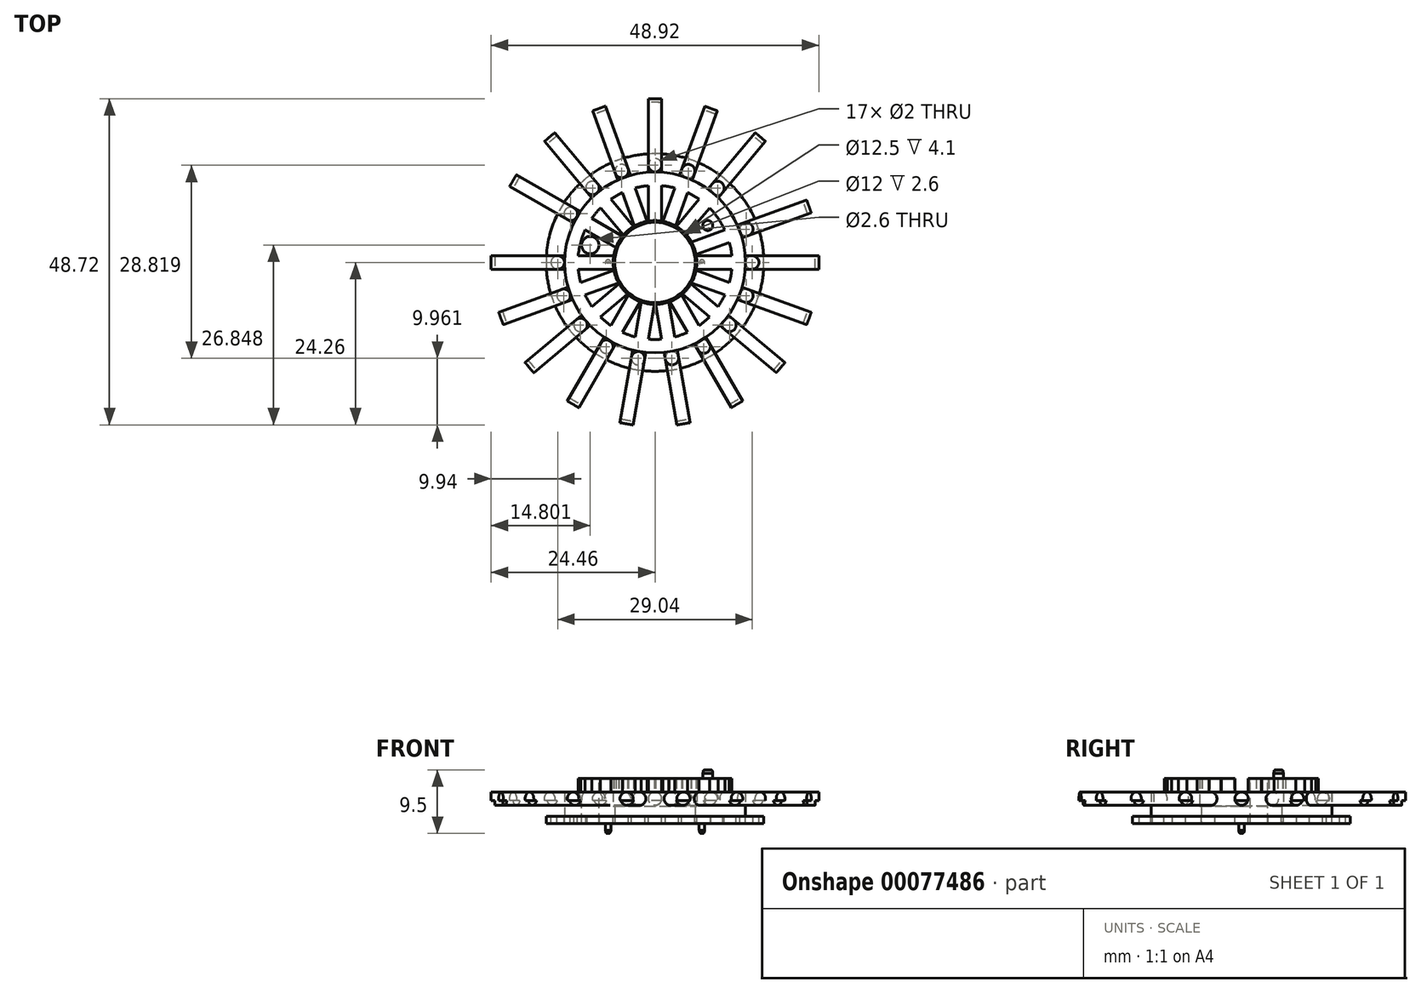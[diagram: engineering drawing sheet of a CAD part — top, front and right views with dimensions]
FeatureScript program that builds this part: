
annotation { "Feature Type Name" : "Feature", "Feature Type Description" : "" }
export const myFeature = defineFeature(function(context is Context, id is Id, definition is map)
    precondition{}
    {
        {
            var Q0;
            Q0=qCreatedBy(makeId("Front.planeOp"),FACE);
            var sketch = newSketch(context, id + "F0", { "sketchPlane" : qUnion([Q0])});
            skLineSegment(sketch, "E0", {"start": v(6, 0) * mm, "end": v(16.25, 0) * mm});
            skLineSegment(sketch, "E1", {"start": v(16.25, 0) * mm, "end": v(16.25, 1.1) * mm});
            skLineSegment(sketch, "E2", {"start": v(16.25, 1.1) * mm, "end": v(13.5, 1.1) * mm});
            skLineSegment(sketch, "E3", {"start": v(13.5, 1.1) * mm, "end": v(13.5, 4.7) * mm});
            skLineSegment(sketch, "E4", {"start": v(13.5, 4.7) * mm, "end": v(11.5, 4.7) * mm});
            skLineSegment(sketch, "E5", {"start": v(11.5, 4.7) * mm, "end": v(11.5, 6.7) * mm});
            skLineSegment(sketch, "E6", {"start": v(11.5, 6.7) * mm, "end": v(6.25, 6.7) * mm});
            skLineSegment(sketch, "E7", {"start": v(6.25, 6.7) * mm, "end": v(6.25, 2.6) * mm});
            skLineSegment(sketch, "E8", {"start": v(6.25, 2.6) * mm, "end": v(6, 2.6) * mm});
            skLineSegment(sketch, "E9", {"start": v(6, 2.6) * mm, "end": v(6, 0) * mm});
            skLineSegment(sketch, "E10", {"start": v(0, 0) * mm, "end": v(0, 6.7) * mm, "construction": true});
            skSolve(sketch);
        }
        {
            var Q0;
            Q0=makeQuery(id+"F0.imprint","IMPRINT",FACE,{"disambiguationData":[TD([[makeQuery(id+"F0.imprint","IMPRINT",EDGE,{"derivedFrom":sQuery(id+"F0.wireOp",EDGE,"E0")}),1.0]])]});
            var Q1;
            Q1=sQuery(id+"F0.wireOp",EDGE,"E10");
            revolve(context, id + "F1", {"entities" : qUnion([Q0]), "axis" : qUnion([Q1]), "revolveType" : RevolveType.FULL});
        }
        {
            var Q0;
            Q0=makeQuery(id+"F1.opRevolve","SWEPT_FACE",FACE,{"disambiguationData":[OSD([sQuery(id+"F0.wireOp",EDGE,"E6")])]});
            cPlane(context, id + "F2", {"entities" : qUnion([Q0]), "cplaneType" : CPlaneType.OFFSET, "offset" : 2 * mm, "oppositeDirection" : true, "width" : 150 * mm, "height" : 150 * mm});
        }
        {
            var Q0;
            Q0=qCreatedBy(id+"F2.planeOp",FACE);
            var sketch = newSketch(context, id + "F3", { "sketchPlane" : qUnion([Q0])});
            skLineSegment(sketch, "E11", {"start": v(-5, 1) * mm, "end": v(-15, 1) * mm});
            skLineSegment(sketch, "E12", {"start": v(-15, 1) * mm, "end": v(-15, -1) * mm});
            skLineSegment(sketch, "E13", {"start": v(-15, -1) * mm, "end": v(-5, -1) * mm});
            skLineSegment(sketch, "E14", {"start": v(-5, 1) * mm, "end": v(-5, -1) * mm});
            skLineSegment(sketch, "E15.1.0", {"start": v(-5.04, -0.77) * mm, "end": v(-14.44, -4.2) * mm});
            skLineSegment(sketch, "E15.1.1", {"start": v(-13.75, -6.07) * mm, "end": v(-4.36, -2.65) * mm});
            skLineSegment(sketch, "E15.1.2", {"start": v(-14.44, -4.2) * mm, "end": v(-13.75, -6.07) * mm});
            skLineSegment(sketch, "E15.1.3", {"start": v(-5.04, -0.77) * mm, "end": v(-4.36, -2.65) * mm});
            skLineSegment(sketch, "E15.2.0", {"start": v(-4.47, -2.45) * mm, "end": v(-12.13, -8.88) * mm});
            skLineSegment(sketch, "E15.2.1", {"start": v(-10.85, -10.4) * mm, "end": v(-3.19, -3.98) * mm});
            skLineSegment(sketch, "E15.2.2", {"start": v(-12.13, -8.88) * mm, "end": v(-10.85, -10.4) * mm});
            skLineSegment(sketch, "E15.2.3", {"start": v(-4.47, -2.45) * mm, "end": v(-3.19, -3.98) * mm});
            skLineSegment(sketch, "E15.3.0", {"start": v(-3.37, -3.83) * mm, "end": v(-8.37, -12.5) * mm});
            skLineSegment(sketch, "E15.3.1", {"start": v(-6.63, -13.5) * mm, "end": v(-1.63, -4.83) * mm});
            skLineSegment(sketch, "E15.3.2", {"start": v(-8.37, -12.5) * mm, "end": v(-6.63, -13.5) * mm});
            skLineSegment(sketch, "E15.3.3", {"start": v(-3.37, -3.83) * mm, "end": v(-1.63, -4.83) * mm});
            skLineSegment(sketch, "E15.4.0", {"start": v(-1.85, -4.75) * mm, "end": v(-3.59, -14.6) * mm});
            skLineSegment(sketch, "E15.4.1", {"start": v(-1.62, -14.95) * mm, "end": v(0.12, -5.1) * mm});
            skLineSegment(sketch, "E15.4.2", {"start": v(-3.59, -14.6) * mm, "end": v(-1.62, -14.95) * mm});
            skLineSegment(sketch, "E15.4.3", {"start": v(-1.85, -4.75) * mm, "end": v(0.12, -5.1) * mm});
            skLineSegment(sketch, "E15.5.0", {"start": v(-0.12, -5.1) * mm, "end": v(1.62, -14.95) * mm});
            skLineSegment(sketch, "E15.5.1", {"start": v(3.59, -14.6) * mm, "end": v(1.85, -4.75) * mm});
            skLineSegment(sketch, "E15.5.2", {"start": v(1.62, -14.95) * mm, "end": v(3.59, -14.6) * mm});
            skLineSegment(sketch, "E15.5.3", {"start": v(-0.12, -5.1) * mm, "end": v(1.85, -4.75) * mm});
            skLineSegment(sketch, "E15.6.0", {"start": v(1.63, -4.83) * mm, "end": v(6.63, -13.5) * mm});
            skLineSegment(sketch, "E15.6.1", {"start": v(8.37, -12.5) * mm, "end": v(3.37, -3.83) * mm});
            skLineSegment(sketch, "E15.6.2", {"start": v(6.63, -13.5) * mm, "end": v(8.37, -12.5) * mm});
            skLineSegment(sketch, "E15.6.3", {"start": v(1.63, -4.83) * mm, "end": v(3.37, -3.83) * mm});
            skLineSegment(sketch, "E15.7.0", {"start": v(3.19, -3.98) * mm, "end": v(10.85, -10.4) * mm});
            skLineSegment(sketch, "E15.7.1", {"start": v(12.13, -8.88) * mm, "end": v(4.47, -2.45) * mm});
            skLineSegment(sketch, "E15.7.2", {"start": v(10.85, -10.4) * mm, "end": v(12.13, -8.88) * mm});
            skLineSegment(sketch, "E15.7.3", {"start": v(3.19, -3.98) * mm, "end": v(4.47, -2.45) * mm});
            skLineSegment(sketch, "E15.8.0", {"start": v(4.36, -2.65) * mm, "end": v(13.75, -6.07) * mm});
            skLineSegment(sketch, "E15.8.1", {"start": v(14.44, -4.2) * mm, "end": v(5.04, -0.77) * mm});
            skLineSegment(sketch, "E15.8.2", {"start": v(13.75, -6.07) * mm, "end": v(14.44, -4.2) * mm});
            skLineSegment(sketch, "E15.8.3", {"start": v(4.36, -2.65) * mm, "end": v(5.04, -0.77) * mm});
            skLineSegment(sketch, "E15.9.0", {"start": v(5, -1) * mm, "end": v(15, -1) * mm});
            skLineSegment(sketch, "E15.9.1", {"start": v(15, 1) * mm, "end": v(5, 1) * mm});
            skLineSegment(sketch, "E15.9.2", {"start": v(15, -1) * mm, "end": v(15, 1) * mm});
            skLineSegment(sketch, "E15.9.3", {"start": v(5, -1) * mm, "end": v(5, 1) * mm});
            skLineSegment(sketch, "E15.10.0", {"start": v(5.04, 0.77) * mm, "end": v(14.44, 4.2) * mm});
            skLineSegment(sketch, "E15.10.1", {"start": v(13.75, 6.07) * mm, "end": v(4.36, 2.65) * mm});
            skLineSegment(sketch, "E15.10.2", {"start": v(14.44, 4.2) * mm, "end": v(13.75, 6.07) * mm});
            skLineSegment(sketch, "E15.10.3", {"start": v(5.04, 0.77) * mm, "end": v(4.36, 2.65) * mm});
            skPoint(sketch, "E15.center", {"position": v(0, 0) * mm});
            skLineSegment(sketch, "E15.anchor1", {"start": v(0, 0) * mm, "end": v(-15, 1) * mm, "construction": true});
            skLineSegment(sketch, "E15.anchor2", {"start": v(0, 0) * mm, "end": v(14.44, 4.2) * mm, "construction": true});
            skLineSegment(sketch, "E16.1.0", {"start": v(-3.83, 3.37) * mm, "end": v(-4.83, 1.63) * mm});
            skLineSegment(sketch, "E16.1.1", {"start": v(-13.5, 6.63) * mm, "end": v(-4.83, 1.63) * mm});
            skLineSegment(sketch, "E16.1.2", {"start": v(-12.5, 8.37) * mm, "end": v(-13.5, 6.63) * mm});
            skLineSegment(sketch, "E16.1.3", {"start": v(-3.83, 3.37) * mm, "end": v(-12.5, 8.37) * mm});
            skLineSegment(sketch, "E16.anchor1", {"start": v(0, 0) * mm, "end": v(-5, -1) * mm, "construction": true});
            skLineSegment(sketch, "E16.anchor2", {"start": v(0, 0) * mm, "end": v(-4.83, 1.63) * mm, "construction": true});
            skLineSegment(sketch, "E17.1.0", {"start": v(-2.45, 4.47) * mm, "end": v(-3.98, 3.19) * mm});
            skLineSegment(sketch, "E17.1.1", {"start": v(-10.4, 10.85) * mm, "end": v(-3.98, 3.19) * mm});
            skLineSegment(sketch, "E17.1.2", {"start": v(-8.88, 12.13) * mm, "end": v(-10.4, 10.85) * mm});
            skLineSegment(sketch, "E17.1.3", {"start": v(-2.45, 4.47) * mm, "end": v(-8.88, 12.13) * mm});
            skLineSegment(sketch, "E17.2.0", {"start": v(-0.77, 5.04) * mm, "end": v(-2.65, 4.36) * mm});
            skLineSegment(sketch, "E17.2.1", {"start": v(-6.07, 13.75) * mm, "end": v(-2.65, 4.36) * mm});
            skLineSegment(sketch, "E17.2.2", {"start": v(-4.2, 14.44) * mm, "end": v(-6.07, 13.75) * mm});
            skLineSegment(sketch, "E17.2.3", {"start": v(-0.77, 5.04) * mm, "end": v(-4.2, 14.44) * mm});
            skLineSegment(sketch, "E17.3.0", {"start": v(1, 5) * mm, "end": v(-1, 5) * mm});
            skLineSegment(sketch, "E17.3.1", {"start": v(-1, 15) * mm, "end": v(-1, 5) * mm});
            skLineSegment(sketch, "E17.3.2", {"start": v(1, 15) * mm, "end": v(-1, 15) * mm});
            skLineSegment(sketch, "E17.3.3", {"start": v(1, 5) * mm, "end": v(1, 15) * mm});
            skLineSegment(sketch, "E17.4.0", {"start": v(2.65, 4.36) * mm, "end": v(0.77, 5.04) * mm});
            skLineSegment(sketch, "E17.4.1", {"start": v(4.2, 14.44) * mm, "end": v(0.77, 5.04) * mm});
            skLineSegment(sketch, "E17.4.2", {"start": v(6.07, 13.75) * mm, "end": v(4.2, 14.44) * mm});
            skLineSegment(sketch, "E17.4.3", {"start": v(2.65, 4.36) * mm, "end": v(6.07, 13.75) * mm});
            skLineSegment(sketch, "E17.5.0", {"start": v(3.98, 3.19) * mm, "end": v(2.45, 4.47) * mm});
            skLineSegment(sketch, "E17.5.1", {"start": v(8.88, 12.13) * mm, "end": v(2.45, 4.47) * mm});
            skLineSegment(sketch, "E17.5.2", {"start": v(10.4, 10.85) * mm, "end": v(8.88, 12.13) * mm});
            skLineSegment(sketch, "E17.5.3", {"start": v(3.98, 3.19) * mm, "end": v(10.4, 10.85) * mm});
            skLineSegment(sketch, "E17.anchor2", {"start": v(0, 0) * mm, "end": v(2.45, 4.47) * mm, "construction": true});
            skSolve(sketch);
        }
        {
            var Q0;
            {var subQ0=sQuery(id+"F3.wireOp",EDGE,"E15.1.3");var subQ1=sQuery(id+"F3.wireOp",EDGE,"E14");var subQ6=sQuery(id+"F3.wireOp",EDGE,"E13");var subQ9=sQuery(id+"F3.wireOp",EDGE,"E11");var subQ12=sQuery(id+"F3.wireOp",EDGE,"E15.10.1");var subQ14=sQuery(id+"F3.wireOp",EDGE,"E15.9.3");var subQ17=sQuery(id+"F3.wireOp",EDGE,"E15.9.1");var subQ19=makeQuery(id+"F3.imprint","INTERSECT",VERTEX,{"derivedFrom":[subQ17,subQ14]});var subQ21=makeQuery(id+"F3.imprint","IMPRINT",EDGE,{"disambiguationData":[TD([[subQ19,1.0]])],"derivedFrom":subQ17});var subQ22=makeQuery(id+"F3.imprint","INTERSECT",VERTEX,{"derivedFrom":[subQ6,subQ1]});var subQ24=makeQuery(id+"F3.imprint","IMPRINT",EDGE,{"disambiguationData":[TD([[subQ22,1.0]])],"derivedFrom":subQ6});var subQ26=sQuery(id+"F3.wireOp",EDGE,"E15.1.1");var subQ28=sQuery(id+"F3.wireOp",EDGE,"E15.2.3");var subQ31=sQuery(id+"F3.wireOp",EDGE,"E15.1.2");var subQ34=makeQuery(id+"F3.imprint","INTERSECT",VERTEX,{"derivedFrom":[subQ26,subQ0]});var subQ36=makeQuery(id+"F3.imprint","IMPRINT",EDGE,{"disambiguationData":[TD([[subQ34,1.0]])],"derivedFrom":subQ26});var subQ37=sQuery(id+"F3.wireOp",EDGE,"E15.3.3");var subQ42=sQuery(id+"F3.wireOp",EDGE,"E15.2.1");var subQ45=sQuery(id+"F3.wireOp",EDGE,"E15.2.2");var subQ46=makeQuery(id+"F3.imprint","INTERSECT",VERTEX,{"derivedFrom":[subQ42,subQ28]});var subQ48=makeQuery(id+"F3.imprint","IMPRINT",EDGE,{"disambiguationData":[TD([[subQ46,1.0]])],"derivedFrom":subQ42});var subQ49=sQuery(id+"F3.wireOp",EDGE,"E15.4.3");var subQ51=sQuery(id+"F3.wireOp",EDGE,"E15.3.2");var subQ52=sQuery(id+"F3.wireOp",EDGE,"E15.3.1");var subQ58=makeQuery(id+"F3.imprint","INTERSECT",VERTEX,{"derivedFrom":[subQ52,subQ37]});var subQ60=makeQuery(id+"F3.imprint","IMPRINT",EDGE,{"disambiguationData":[TD([[subQ58,1.0]])],"derivedFrom":subQ52});var subQ62=sQuery(id+"F3.wireOp",EDGE,"E15.4.1");var subQ64=sQuery(id+"F3.wireOp",EDGE,"E15.5.3");var subQ68=sQuery(id+"F3.wireOp",EDGE,"E15.4.2");var subQ70=makeQuery(id+"F3.imprint","INTERSECT",VERTEX,{"derivedFrom":[subQ62,subQ49]});var subQ72=makeQuery(id+"F3.imprint","IMPRINT",EDGE,{"disambiguationData":[TD([[subQ70,1.0]])],"derivedFrom":subQ62});var subQ74=sQuery(id+"F3.wireOp",EDGE,"E15.5.1");var subQ76=sQuery(id+"F3.wireOp",EDGE,"E15.6.3");var subQ80=sQuery(id+"F3.wireOp",EDGE,"E15.5.2");var subQ82=makeQuery(id+"F3.imprint","INTERSECT",VERTEX,{"derivedFrom":[subQ74,subQ64]});var subQ84=makeQuery(id+"F3.imprint","IMPRINT",EDGE,{"disambiguationData":[TD([[subQ82,1.0]])],"derivedFrom":subQ74});var subQ85=sQuery(id+"F3.wireOp",EDGE,"E15.7.3");var subQ90=sQuery(id+"F3.wireOp",EDGE,"E15.6.1");var subQ93=sQuery(id+"F3.wireOp",EDGE,"E15.6.2");var subQ94=makeQuery(id+"F3.imprint","INTERSECT",VERTEX,{"derivedFrom":[subQ90,subQ76]});var subQ96=makeQuery(id+"F3.imprint","IMPRINT",EDGE,{"disambiguationData":[TD([[subQ94,1.0]])],"derivedFrom":subQ90});var subQ97=sQuery(id+"F3.wireOp",EDGE,"E15.8.3");var subQ102=sQuery(id+"F3.wireOp",EDGE,"E15.7.1");var subQ105=sQuery(id+"F3.wireOp",EDGE,"E15.7.2");var subQ106=makeQuery(id+"F3.imprint","INTERSECT",VERTEX,{"derivedFrom":[subQ102,subQ85]});var subQ108=makeQuery(id+"F3.imprint","IMPRINT",EDGE,{"disambiguationData":[TD([[subQ106,1.0]])],"derivedFrom":subQ102});var subQ113=sQuery(id+"F3.wireOp",EDGE,"E15.8.1");var subQ116=sQuery(id+"F3.wireOp",EDGE,"E15.8.2");var subQ117=makeQuery(id+"F3.imprint","INTERSECT",VERTEX,{"derivedFrom":[subQ113,subQ97]});var subQ119=makeQuery(id+"F3.imprint","IMPRINT",EDGE,{"disambiguationData":[TD([[subQ117,1.0]])],"derivedFrom":subQ113});var subQ123=sQuery(id+"F3.wireOp",EDGE,"E15.9.2");var subQ125=sQuery(id+"F3.wireOp",EDGE,"E16.1.3");var subQ127=sQuery(id+"F3.wireOp",EDGE,"E17.1.0");var subQ131=sQuery(id+"F3.wireOp",EDGE,"E16.1.0");var subQ134=sQuery(id+"F3.wireOp",EDGE,"E16.1.1");var subQ136=sQuery(id+"F3.wireOp",EDGE,"E17.5.2");var subQ138=sQuery(id+"F3.wireOp",EDGE,"E17.4.3");var subQ141=sQuery(id+"F3.wireOp",EDGE,"E17.4.0");var subQ143=makeQuery(id+"F3.imprint","INTERSECT",VERTEX,{"derivedFrom":[subQ141,subQ138]});var subQ145=makeQuery(id+"F3.imprint","IMPRINT",EDGE,{"disambiguationData":[TD([[subQ143,-1.0]])],"derivedFrom":subQ141});var subQ146=sQuery(id+"F3.wireOp",EDGE,"E17.1.3");var subQ149=sQuery(id+"F3.wireOp",EDGE,"E17.1.2");var subQ150=sQuery(id+"F3.wireOp",EDGE,"E17.2.0");var subQ154=makeQuery(id+"F3.imprint","INTERSECT",VERTEX,{"derivedFrom":[subQ131,subQ125]});var subQ157=makeQuery(id+"F3.imprint","IMPRINT",EDGE,{"disambiguationData":[TD([[subQ154,-1.0]])],"derivedFrom":subQ131});var subQ159=sQuery(id+"F3.wireOp",EDGE,"E17.2.3");var subQ161=sQuery(id+"F3.wireOp",EDGE,"E17.3.0");var subQ166=sQuery(id+"F3.wireOp",EDGE,"E17.2.2");var subQ167=makeQuery(id+"F3.imprint","INTERSECT",VERTEX,{"derivedFrom":[subQ127,subQ146]});var subQ169=makeQuery(id+"F3.imprint","IMPRINT",EDGE,{"disambiguationData":[TD([[subQ167,-1.0]])],"derivedFrom":subQ127});var subQ171=sQuery(id+"F3.wireOp",EDGE,"E17.3.3");var subQ175=sQuery(id+"F3.wireOp",EDGE,"E17.3.2");var subQ178=makeQuery(id+"F3.imprint","INTERSECT",VERTEX,{"derivedFrom":[subQ150,subQ159]});var subQ180=makeQuery(id+"F3.imprint","IMPRINT",EDGE,{"disambiguationData":[TD([[subQ178,-1.0]])],"derivedFrom":subQ150});var subQ184=sQuery(id+"F3.wireOp",EDGE,"E17.4.2");var subQ185=makeQuery(id+"F3.imprint","INTERSECT",VERTEX,{"derivedFrom":[subQ161,subQ171]});var subQ187=makeQuery(id+"F3.imprint","IMPRINT",EDGE,{"disambiguationData":[TD([[subQ185,-1.0]])],"derivedFrom":subQ161});Q0=qUnion([makeQuery(id+"F3.imprint","IMPRINT",FACE,{"disambiguationData":[TD([[makeQuery(id+"F3.imprint","IMPRINT",EDGE,{"derivedFrom":subQ9}),1.0]])]}),makeQuery(id+"F3.imprint","IMPRINT",FACE,{"disambiguationData":[TD([[makeQuery(id+"F3.imprint","IMPRINT",EDGE,{"derivedFrom":subQ12}),1.0]])]}),makeQuery(id+"F3.imprint","IMPRINT",FACE,{"disambiguationData":[TD([[subQ24,1.0]])]}),makeQuery(id+"F3.imprint","IMPRINT",FACE,{"disambiguationData":[TD([[makeQuery(id+"F3.imprint","IMPRINT",EDGE,{"derivedFrom":subQ31}),1.0]])]}),makeQuery(id+"F3.imprint","IMPRINT",FACE,{"disambiguationData":[TD([[subQ36,1.0]])]}),makeQuery(id+"F3.imprint","IMPRINT",FACE,{"disambiguationData":[TD([[makeQuery(id+"F3.imprint","IMPRINT",EDGE,{"derivedFrom":subQ45}),1.0]])]}),makeQuery(id+"F3.imprint","IMPRINT",FACE,{"disambiguationData":[TD([[subQ48,1.0]])]}),makeQuery(id+"F3.imprint","IMPRINT",FACE,{"disambiguationData":[TD([[makeQuery(id+"F3.imprint","IMPRINT",EDGE,{"derivedFrom":subQ51}),1.0]])]}),makeQuery(id+"F3.imprint","IMPRINT",FACE,{"disambiguationData":[TD([[subQ60,1.0]])]}),makeQuery(id+"F3.imprint","IMPRINT",FACE,{"disambiguationData":[TD([[makeQuery(id+"F3.imprint","IMPRINT",EDGE,{"derivedFrom":subQ68}),1.0]])]}),makeQuery(id+"F3.imprint","IMPRINT",FACE,{"disambiguationData":[TD([[subQ72,1.0]])]}),makeQuery(id+"F3.imprint","IMPRINT",FACE,{"disambiguationData":[TD([[makeQuery(id+"F3.imprint","IMPRINT",EDGE,{"derivedFrom":subQ80}),1.0]])]}),makeQuery(id+"F3.imprint","IMPRINT",FACE,{"disambiguationData":[TD([[subQ84,1.0]])]}),makeQuery(id+"F3.imprint","IMPRINT",FACE,{"disambiguationData":[TD([[makeQuery(id+"F3.imprint","IMPRINT",EDGE,{"derivedFrom":subQ93}),1.0]])]}),makeQuery(id+"F3.imprint","IMPRINT",FACE,{"disambiguationData":[TD([[subQ96,1.0]])]}),makeQuery(id+"F3.imprint","IMPRINT",FACE,{"disambiguationData":[TD([[makeQuery(id+"F3.imprint","IMPRINT",EDGE,{"derivedFrom":subQ105}),1.0]])]}),makeQuery(id+"F3.imprint","IMPRINT",FACE,{"disambiguationData":[TD([[subQ108,1.0]])]}),makeQuery(id+"F3.imprint","IMPRINT",FACE,{"disambiguationData":[TD([[makeQuery(id+"F3.imprint","IMPRINT",EDGE,{"derivedFrom":subQ116}),1.0]])]}),makeQuery(id+"F3.imprint","IMPRINT",FACE,{"disambiguationData":[TD([[subQ119,1.0]])]}),makeQuery(id+"F3.imprint","IMPRINT",FACE,{"disambiguationData":[TD([[makeQuery(id+"F3.imprint","IMPRINT",EDGE,{"derivedFrom":subQ123}),1.0]])]}),makeQuery(id+"F3.imprint","IMPRINT",FACE,{"disambiguationData":[TD([[subQ21,1.0]])]}),makeQuery(id+"F3.imprint","IMPRINT",FACE,{"disambiguationData":[TD([[makeQuery(id+"F3.imprint","IMPRINT",EDGE,{"derivedFrom":subQ134}),1.0]])]}),makeQuery(id+"F3.imprint","IMPRINT",FACE,{"disambiguationData":[TD([[makeQuery(id+"F3.imprint","IMPRINT",EDGE,{"derivedFrom":subQ136}),1.0]])]}),makeQuery(id+"F3.imprint","IMPRINT",FACE,{"disambiguationData":[TD([[makeQuery(id+"F3.imprint","IMPRINT",EDGE,{"derivedFrom":subQ149}),1.0]])]}),makeQuery(id+"F3.imprint","IMPRINT",FACE,{"disambiguationData":[TD([[subQ157,-1.0]])]}),makeQuery(id+"F3.imprint","IMPRINT",FACE,{"disambiguationData":[TD([[makeQuery(id+"F3.imprint","IMPRINT",EDGE,{"derivedFrom":subQ166}),1.0]])]}),makeQuery(id+"F3.imprint","IMPRINT",FACE,{"disambiguationData":[TD([[subQ169,-1.0]])]}),makeQuery(id+"F3.imprint","IMPRINT",FACE,{"disambiguationData":[TD([[makeQuery(id+"F3.imprint","IMPRINT",EDGE,{"derivedFrom":subQ175}),1.0]])]}),makeQuery(id+"F3.imprint","IMPRINT",FACE,{"disambiguationData":[TD([[subQ180,-1.0]])]}),makeQuery(id+"F3.imprint","IMPRINT",FACE,{"disambiguationData":[TD([[makeQuery(id+"F3.imprint","IMPRINT",EDGE,{"derivedFrom":subQ184}),1.0]])]}),makeQuery(id+"F3.imprint","IMPRINT",FACE,{"disambiguationData":[TD([[subQ187,-1.0]])]}),makeQuery(id+"F3.imprint","IMPRINT",FACE,{"disambiguationData":[TD([[subQ145,-1.0]])]})]);}
            extrude(context, id + "F4", {"entities" : qUnion([Q0]), "operationType" : NewBodyOperationType.REMOVE, "endBound" : BoundingType.THROUGH_ALL, "depth" : 25 * mm});
        }
        {
            var Q0;
            Q0=makeQuery(id+"F1.opRevolve","SWEPT_FACE",FACE,{"disambiguationData":[OSD([sQuery(id+"F0.wireOp",EDGE,"E2")])]});
            var sketch = newSketch(context, id + "F5", { "sketchPlane" : qUnion([Q0])});
            skCircle(sketch, "E18", {"center": v(0, 0) * mm, "radius": 14.52 * mm, "construction": true});
            skCircle(sketch, "E19", {"center": v(-14.52, 0) * mm, "radius": 1 * mm});
            skCircle(sketch, "E20.1.0", {"center": v(-13.64, -4.97) * mm, "radius": 1 * mm});
            skCircle(sketch, "E20.2.0", {"center": v(-11.12, -9.33) * mm, "radius": 1 * mm});
            skCircle(sketch, "E20.3.0", {"center": v(-7.26, -12.57) * mm, "radius": 1 * mm});
            skCircle(sketch, "E20.4.0", {"center": v(-2.52, -14.3) * mm, "radius": 1 * mm});
            skCircle(sketch, "E20.5.0", {"center": v(2.52, -14.3) * mm, "radius": 1 * mm});
            skCircle(sketch, "E20.6.0", {"center": v(7.26, -12.57) * mm, "radius": 1 * mm});
            skCircle(sketch, "E20.7.0", {"center": v(11.12, -9.33) * mm, "radius": 1 * mm});
            skCircle(sketch, "E20.8.0", {"center": v(13.64, -4.97) * mm, "radius": 1 * mm});
            skCircle(sketch, "E20.9.0", {"center": v(14.52, 0) * mm, "radius": 1 * mm});
            skCircle(sketch, "E20.10.0", {"center": v(13.64, 4.97) * mm, "radius": 1 * mm});
            skLineSegment(sketch, "E20.anchor1", {"start": v(0, 0) * mm, "end": v(-14.52, 0) * mm, "construction": true});
            skLineSegment(sketch, "E20.anchor2", {"start": v(0, 0) * mm, "end": v(13.64, 4.97) * mm, "construction": true});
            skCircle(sketch, "E21.1.0", {"center": v(-12.57, 7.26) * mm, "radius": 1 * mm});
            skLineSegment(sketch, "E21.anchor2", {"start": v(0, 0) * mm, "end": v(-12.57, 7.26) * mm, "construction": true});
            skCircle(sketch, "E22.1.0", {"center": v(-9.33, 11.12) * mm, "radius": 1 * mm});
            skCircle(sketch, "E22.2.0", {"center": v(-4.97, 13.64) * mm, "radius": 1 * mm});
            skCircle(sketch, "E22.3.0", {"center": v(0, 14.52) * mm, "radius": 1 * mm});
            skCircle(sketch, "E22.4.0", {"center": v(4.97, 13.64) * mm, "radius": 1 * mm});
            skCircle(sketch, "E22.5.0", {"center": v(9.33, 11.12) * mm, "radius": 1 * mm});
            skLineSegment(sketch, "E22.anchor2", {"start": v(0, 0) * mm, "end": v(9.33, 11.12) * mm, "construction": true});
            skSolve(sketch);
        }
        {
            var Q0;
            {Q0=qUnion([makeQuery(id+"F5.imprint","IMPRINT",FACE,{"disambiguationData":[TD([[makeQuery(id+"F5.imprint","IMPRINT",EDGE,{"derivedFrom":sQuery(id+"F5.wireOp",EDGE,"E19")}),1.0]])]}),makeQuery(id+"F5.imprint","IMPRINT",FACE,{"disambiguationData":[TD([[makeQuery(id+"F5.imprint","IMPRINT",EDGE,{"derivedFrom":sQuery(id+"F5.wireOp",EDGE,"E20.1.0")}),1.0]])]}),makeQuery(id+"F5.imprint","IMPRINT",FACE,{"disambiguationData":[TD([[makeQuery(id+"F5.imprint","IMPRINT",EDGE,{"derivedFrom":sQuery(id+"F5.wireOp",EDGE,"E20.2.0")}),1.0]])]}),makeQuery(id+"F5.imprint","IMPRINT",FACE,{"disambiguationData":[TD([[makeQuery(id+"F5.imprint","IMPRINT",EDGE,{"derivedFrom":sQuery(id+"F5.wireOp",EDGE,"E20.3.0")}),1.0]])]}),makeQuery(id+"F5.imprint","IMPRINT",FACE,{"disambiguationData":[TD([[makeQuery(id+"F5.imprint","IMPRINT",EDGE,{"derivedFrom":sQuery(id+"F5.wireOp",EDGE,"E20.4.0")}),1.0]])]}),makeQuery(id+"F5.imprint","IMPRINT",FACE,{"disambiguationData":[TD([[makeQuery(id+"F5.imprint","IMPRINT",EDGE,{"derivedFrom":sQuery(id+"F5.wireOp",EDGE,"E20.5.0")}),1.0]])]}),makeQuery(id+"F5.imprint","IMPRINT",FACE,{"disambiguationData":[TD([[makeQuery(id+"F5.imprint","IMPRINT",EDGE,{"derivedFrom":sQuery(id+"F5.wireOp",EDGE,"E20.6.0")}),1.0]])]}),makeQuery(id+"F5.imprint","IMPRINT",FACE,{"disambiguationData":[TD([[makeQuery(id+"F5.imprint","IMPRINT",EDGE,{"derivedFrom":sQuery(id+"F5.wireOp",EDGE,"E20.7.0")}),1.0]])]}),makeQuery(id+"F5.imprint","IMPRINT",FACE,{"disambiguationData":[TD([[makeQuery(id+"F5.imprint","IMPRINT",EDGE,{"derivedFrom":sQuery(id+"F5.wireOp",EDGE,"E20.8.0")}),1.0]])]}),makeQuery(id+"F5.imprint","IMPRINT",FACE,{"disambiguationData":[TD([[makeQuery(id+"F5.imprint","IMPRINT",EDGE,{"derivedFrom":sQuery(id+"F5.wireOp",EDGE,"E20.9.0")}),1.0]])]}),makeQuery(id+"F5.imprint","IMPRINT",FACE,{"disambiguationData":[TD([[makeQuery(id+"F5.imprint","IMPRINT",EDGE,{"derivedFrom":sQuery(id+"F5.wireOp",EDGE,"E20.10.0")}),1.0]])]}),makeQuery(id+"F5.imprint","IMPRINT",FACE,{"disambiguationData":[TD([[makeQuery(id+"F5.imprint","IMPRINT",EDGE,{"derivedFrom":sQuery(id+"F5.wireOp",EDGE,"E21.1.0")}),1.0]])]}),makeQuery(id+"F5.imprint","IMPRINT",FACE,{"disambiguationData":[TD([[makeQuery(id+"F5.imprint","IMPRINT",EDGE,{"derivedFrom":sQuery(id+"F5.wireOp",EDGE,"E22.1.0")}),1.0]])]}),makeQuery(id+"F5.imprint","IMPRINT",FACE,{"disambiguationData":[TD([[makeQuery(id+"F5.imprint","IMPRINT",EDGE,{"derivedFrom":sQuery(id+"F5.wireOp",EDGE,"E22.2.0")}),1.0]])]}),makeQuery(id+"F5.imprint","IMPRINT",FACE,{"disambiguationData":[TD([[makeQuery(id+"F5.imprint","IMPRINT",EDGE,{"derivedFrom":sQuery(id+"F5.wireOp",EDGE,"E22.3.0")}),1.0]])]}),makeQuery(id+"F5.imprint","IMPRINT",FACE,{"disambiguationData":[TD([[makeQuery(id+"F5.imprint","IMPRINT",EDGE,{"derivedFrom":sQuery(id+"F5.wireOp",EDGE,"E22.4.0")}),1.0]])]}),makeQuery(id+"F5.imprint","IMPRINT",FACE,{"disambiguationData":[TD([[makeQuery(id+"F5.imprint","IMPRINT",EDGE,{"derivedFrom":sQuery(id+"F5.wireOp",EDGE,"E22.5.0")}),1.0]])]})]);}
            extrude(context, id + "F6", {"entities" : qUnion([Q0]), "operationType" : NewBodyOperationType.REMOVE, "endBound" : BoundingType.THROUGH_ALL, "oppositeDirection" : true, "depth" : 25 * mm});
        }
        {
            var Q0;
            Q0=makeQuery(id+"F4.boolean.opBoolean","SPLIT",FACE,{"disambiguationData":[TD([makeQuery(id+"F4.opExtrude","SWEPT_FACE",FACE,{"disambiguationData":[OSD([sQuery(id+"F3.wireOp",EDGE,"E11")])]})])],"derivedFrom":makeQuery(id+"F1.opRevolve","SWEPT_FACE",FACE,{"disambiguationData":[OSD([sQuery(id+"F0.wireOp",EDGE,"E6")])]})});
            var sketch = newSketch(context, id + "F7", { "sketchPlane" : qUnion([Q0])});
            skCircle(sketch, "E23", {"center": v(-9.66, 2.59) * mm, "radius": 1.3 * mm});
            skLineSegment(sketch, "E24", {"start": v(-9.66, 2.59) * mm, "end": v(0, 0) * mm, "construction": true});
            skSolve(sketch);
        }
        {
            var Q0;
            Q0=makeQuery(id+"F7.imprint","IMPRINT",FACE,{"disambiguationData":[TD([[makeQuery(id+"F7.imprint","IMPRINT",EDGE,{"derivedFrom":sQuery(id+"F7.wireOp",EDGE,"E23")}),1.0]])]});
            extrude(context, id + "F8", {"entities" : qUnion([Q0]), "operationType" : NewBodyOperationType.REMOVE, "endBound" : BoundingType.THROUGH_ALL, "oppositeDirection" : true, "depth" : 25 * mm});
        }
        {
            var Q0;
            Q0=makeQuery(id+"F4.boolean.opBoolean","SPLIT",FACE,{"disambiguationData":[TD([makeQuery(id+"F4.opExtrude","SWEPT_FACE",FACE,{"disambiguationData":[OSD([sQuery(id+"F3.wireOp",EDGE,"E15.10.1")])]})])],"derivedFrom":makeQuery(id+"F1.opRevolve","SWEPT_FACE",FACE,{"disambiguationData":[OSD([sQuery(id+"F0.wireOp",EDGE,"E6")])]})});
            var sketch = newSketch(context, id + "F9", { "sketchPlane" : qUnion([Q0])});
            skCircle(sketch, "E25", {"center": v(7.88, 5.52) * mm, "radius": 0.75 * mm});
            skLineSegment(sketch, "E26", {"start": v(7.88, 5.52) * mm, "end": v(0, 0) * mm, "construction": true});
            skSolve(sketch);
        }
        {
            var Q0;
            Q0=makeQuery(id+"F9.imprint","IMPRINT",FACE,{"disambiguationData":[TD([[makeQuery(id+"F9.imprint","IMPRINT",EDGE,{"derivedFrom":sQuery(id+"F9.wireOp",EDGE,"E25")}),1.0]])]});
            extrude(context, id + "F10", {"entities" : qUnion([Q0]), "operationType" : NewBodyOperationType.ADD, "depth" : 1.3 * mm});
        }
        {
            var Q0;
            Q0=makeQuery(id+"F1.opRevolve","SWEPT_FACE",FACE,{"disambiguationData":[OSD([sQuery(id+"F0.wireOp",EDGE,"E0")])]});
            var sketch = newSketch(context, id + "F11", { "sketchPlane" : qUnion([Q0])});
            skCircle(sketch, "E27", {"center": v(0, 0) * mm, "radius": 7 * mm, "construction": true});
            skCircle(sketch, "E28", {"center": v(-7, 0) * mm, "radius": 0.4 * mm});
            skCircle(sketch, "E29", {"center": v(7, 0) * mm, "radius": 0.4 * mm});
            skSolve(sketch);
        }
        {
            var Q0;
            {Q0=qUnion([makeQuery(id+"F11.imprint","IMPRINT",FACE,{"disambiguationData":[TD([[makeQuery(id+"F11.imprint","IMPRINT",EDGE,{"derivedFrom":sQuery(id+"F11.wireOp",EDGE,"E28")}),1.0]])]}),makeQuery(id+"F11.imprint","IMPRINT",FACE,{"disambiguationData":[TD([[makeQuery(id+"F11.imprint","IMPRINT",EDGE,{"derivedFrom":sQuery(id+"F11.wireOp",EDGE,"E29")}),1.0]])]})]);}
            extrude(context, id + "F12", {"entities" : qUnion([Q0]), "operationType" : NewBodyOperationType.ADD, "depth" : 1.5 * mm});
        }
        {
            var Q0;
            Q0=makeQuery(id+"F10.opExtrude","CAP_EDGE",EDGE,{"disambiguationData":[OSD([sQuery(id+"F9.wireOp",EDGE,"E25")])],"isStart":false});
            chamfer(context, id + "F13", {"entities" : qUnion([Q0]), "chamferType" : ChamferType.OFFSET_ANGLE, "width" : 0.5 * mm, "oppositeDirection" : true, "angle" : 12 * degree, "tangentPropagation" : true});
        }
        {
            var Q0;
            {var subQ0=sQuery(id+"F9.wireOp",EDGE,"E25");Q0=makeQuery(id+"F13.opChamfer","BLEND_EDGE",EDGE,{"blendedFrom":[makeQuery(id+"F10.opExtrude","CAP_EDGE",EDGE,{"disambiguationData":[OSD([subQ0])],"isStart":false}),makeQuery(id+"F10.opExtrude","CAP_FACE",FACE,{"disambiguationData":[OSD([subQ0])],"isStart":false})],"blendedInto":[makeQuery(id+"F10.opExtrude","CAP_FACE",FACE,{"disambiguationData":[OSD([subQ0])],"isStart":false})]});}
            fillet(context, id + "F14", {"entities" : qUnion([Q0]), "radius" : 0.2 * mm, "tangentPropagation" : true, "rho" : 0.3, "crossSection" : FilletCrossSection.CONIC, "allowEdgeOverflow" : false});
        }
        {
            var Q0;
            Q0=makeQuery(id+"F12.opExtrude","CAP_EDGE",EDGE,{"disambiguationData":[OSD([sQuery(id+"F11.wireOp",EDGE,"E28")])],"isStart":false});
            var Q1;
            Q1=makeQuery(id+"F12.opExtrude","CAP_EDGE",EDGE,{"disambiguationData":[OSD([sQuery(id+"F11.wireOp",EDGE,"E29")])],"isStart":false});
            chamfer(context, id + "F15", {"entities" : qUnion([Q0, Q1]), "chamferType" : ChamferType.OFFSET_ANGLE, "width" : 0.5 * mm, "oppositeDirection" : true, "angle" : 12 * degree, "tangentPropagation" : true});
        }
        {
            var Q0;
            {var subQ0=sQuery(id+"F11.wireOp",EDGE,"E29");Q0=makeQuery(id+"F15.opChamfer","BLEND_EDGE",EDGE,{"blendedFrom":[makeQuery(id+"F12.opExtrude","CAP_EDGE",EDGE,{"disambiguationData":[OSD([subQ0])],"isStart":false}),makeQuery(id+"F12.opExtrude","CAP_FACE",FACE,{"disambiguationData":[OSD([subQ0])],"isStart":false})],"blendedInto":[makeQuery(id+"F12.opExtrude","CAP_FACE",FACE,{"disambiguationData":[OSD([subQ0])],"isStart":false})]});}
            var Q1;
            {var subQ0=sQuery(id+"F11.wireOp",EDGE,"E28");Q1=makeQuery(id+"F15.opChamfer","BLEND_EDGE",EDGE,{"blendedFrom":[makeQuery(id+"F12.opExtrude","CAP_EDGE",EDGE,{"disambiguationData":[OSD([subQ0])],"isStart":false}),makeQuery(id+"F12.opExtrude","CAP_FACE",FACE,{"disambiguationData":[OSD([subQ0])],"isStart":false})],"blendedInto":[makeQuery(id+"F12.opExtrude","CAP_FACE",FACE,{"disambiguationData":[OSD([subQ0])],"isStart":false})]});}
            fillet(context, id + "F16", {"entities" : qUnion([Q0, Q1]), "radius" : 0.2 * mm, "tangentPropagation" : true, "rho" : 0.3, "crossSection" : FilletCrossSection.CONIC, "allowEdgeOverflow" : false});
        }
        {
            var Q0;
            Q0=qCreatedBy(id+"F2.planeOp",FACE);
            cPlane(context, id + "F17", {"entities" : qUnion([Q0]), "cplaneType" : CPlaneType.OFFSET, "offset" : 1 * mm, "oppositeDirection" : true, "width" : 150 * mm, "height" : 150 * mm});
        }
        {
            var Q0;
            Q0=qCreatedBy(id+"F17.planeOp",FACE);
            var sketch = newSketch(context, id + "F18", { "sketchPlane" : qUnion([Q0])});
            skLineSegment(sketch, "E30.bottom", {"start": v(-24.46, 1) * mm, "end": v(-13.46, 1) * mm});
            skLineSegment(sketch, "E30.top", {"start": v(-24.46, 0) * mm, "end": v(-13.46, 0) * mm});
            skLineSegment(sketch, "E30.left", {"start": v(-24.46, 1) * mm, "end": v(-24.46, 0) * mm});
            skLineSegment(sketch, "E30.right", {"start": v(-13.46, 1) * mm, "end": v(-13.46, 0) * mm});
            skSolve(sketch);
        }
        {
            var Q0;
            Q0=makeQuery(id+"F18.imprint","IMPRINT",FACE,{"disambiguationData":[TD([[makeQuery(id+"F18.imprint","IMPRINT",EDGE,{"derivedFrom":sQuery(id+"F18.wireOp",EDGE,"E30.bottom")}),-1.0]])]});
            var Q1;
            Q1=sQuery(id+"F18.wireOp",EDGE,"E30.top");
            revolve(context, id + "F19", {"entities" : qUnion([Q0]), "axis" : qUnion([Q1]), "revolveType" : RevolveType.FULL});
        }
        {
            var Q0;
            Q0=makeQuery(id+"F19.opRevolve","SWEPT_BODY",BODY,{"disambiguationData":[OSD([sQuery(id+"F18.wireOp",EDGE,"E30.bottom"),sQuery(id+"F18.wireOp",EDGE,"E30.top"),sQuery(id+"F18.wireOp",EDGE,"E30.left"),sQuery(id+"F18.wireOp",EDGE,"E30.right")])]});
            var Q1;
            Q1=sQuery(id+"F0.wireOp",EDGE,"E10");
            circularPattern(context, id + "F20", {"entities" : qUnion([Q0]), "axis" : qUnion([Q1]), "angle" : 20 * degree, "instanceCount" : round(11)});
        }
        {
            var Q0;
            Q0=makeQuery(id+"F19.opRevolve","SWEPT_BODY",BODY,{"disambiguationData":[OSD([sQuery(id+"F18.wireOp",EDGE,"E30.bottom"),sQuery(id+"F18.wireOp",EDGE,"E30.top"),sQuery(id+"F18.wireOp",EDGE,"E30.left"),sQuery(id+"F18.wireOp",EDGE,"E30.right")])]});
            var Q1;
            Q1=sQuery(id+"F0.wireOp",EDGE,"E10");
            transform(context, id + "F21", {"entities" : qUnion([Q0]), "transformType" : TransformType.ROTATION, "transformAxis" : qUnion([Q1]), "angle" : 30 * degree, "oppositeDirection" : true, "makeCopy" : true});
        }
        {
            var Q0;
            Q0=makeQuery(id+"F21.opPattern","COPY",FACE,{"derivedFrom":makeQuery(id+"F19.opRevolve","SWEPT_FACE",FACE,{"disambiguationData":[OSD([sQuery(id+"F18.wireOp",EDGE,"E30.bottom")])]}),"instanceName":"1"});
            var Q1;
            Q1=makeQuery(id+"F21.opPattern","COPY",BODY,{"derivedFrom":makeQuery(id+"F19.opRevolve","SWEPT_BODY",BODY,{"disambiguationData":[OSD([sQuery(id+"F18.wireOp",EDGE,"E30.bottom"),sQuery(id+"F18.wireOp",EDGE,"E30.top"),sQuery(id+"F18.wireOp",EDGE,"E30.left"),sQuery(id+"F18.wireOp",EDGE,"E30.right")])]}),"instanceName":"1"});
            var Q2;
            Q2=sQuery(id+"F0.wireOp",EDGE,"E10");
            circularPattern(context, id + "F22", {"entities" : qUnion([Q1]), "axis" : qUnion([Q2]), "angle" : 20 * degree, "instanceCount" : round(6), "oppositeDirection" : true});
        }
        {
            var Q0;
            Q0=makeQuery(id+"F4.boolean.opBoolean","SPLIT",FACE,{"disambiguationData":[TD([makeQuery(id+"F4.opExtrude","SWEPT_FACE",FACE,{"disambiguationData":[OSD([sQuery(id+"F3.wireOp",EDGE,"E17.3.3")])]})])],"derivedFrom":makeQuery(id+"F1.opRevolve","SWEPT_FACE",FACE,{"disambiguationData":[OSD([sQuery(id+"F0.wireOp",EDGE,"E6")])]})});
            cPlane(context, id + "F23", {"entities" : qUnion([Q0]), "cplaneType" : CPlaneType.OFFSET, "offset" : 4 * mm, "oppositeDirection" : true, "width" : 150 * mm, "height" : 150 * mm});
        }
        {
            var Q0;
            Q0=qCreatedBy(id+"F23.planeOp",FACE);
            var sketch = newSketch(context, id + "F24", { "sketchPlane" : qUnion([Q0])});
            skCircle(sketch, "E31", {"center": v(0, 0) * mm, "radius": 24.5 * mm});
            skCircle(sketch, "E32", {"center": v(0, 0) * mm, "radius": 23.9 * mm});
            skSolve(sketch);
        }
        {
            var Q0;
            Q0=makeQuery(id+"F24.imprint","IMPRINT",FACE,{"disambiguationData":[TD([[makeQuery(id+"F24.imprint","IMPRINT",EDGE,{"derivedFrom":sQuery(id+"F24.wireOp",EDGE,"E31")}),1.0]])]});
            extrude(context, id + "F25", {"entities" : qUnion([Q0]), "operationType" : NewBodyOperationType.REMOVE, "depth" : 0.7 * mm});
        }
    });
